# Revit family: 02-75-006 DN040-400
name_source: partatom
category: Pipe Accessories
units: mm (PartAtom-declared; Revit-internal decimal feet)

## family parameters
Always vertical = Yes
Cut with Voids When Loaded = No
Part Type = Valve - Breaks Into
Round Connector Dimension = Use Diameter
Shared = No
Work Plane-Based = No

## types (15) — shared parameters
1 = 1 mm  [stored 0.00328084 ft]
2 = 2 mm  [stored 0.00656168 ft]
5 = 5 mm  [stored 0.0164042 ft]
DN040_PN10/16 = 02-040-75-514649003
DN050_PN10/16 = 02-050-75-514649003
DN060/065_PN10/16 = 02-065-75-5L4649003
DN080_DIN1882 = 02-080-75-514649003
DN080_PN10/16 = 02-080-75-534649003
DN100_PN10/16 = 02-100-75-514649003
DN125_PN10/16 = 02-125-75-514649003
DN150_PN10/16 = 02-150-75-514649003
DN200_PN10 = 02-200-75-504649003
DN200_PN16 = 02-200-75-514649003
DN250_PN10 = 02-250-75-504649003
DN250_PN16 = 02-250-75-514649003
DN300_PN10 = 02-300-75-504647003
DN300_PN16 = 02-300-75-514647003
DN400_PN10 = 02-400-75-50464
DN400_PN16 = 02-400-75-51464
Description_ = AVK GATE VALVE, FLANGED, PN10/16
F = 14 mm  [stored 0.0459318 ft]
F1 = 15 mm  [stored 0.0492126 ft]
Search_table = 02-75-006 DN040-400
URL_product_pages = https://www.avkvalves.com
zero-valued in all types: Default Elevation

## per-type parameters (varying)
- DN040_PN10/16: Body_FL_L=60 mm; Body_FL_T=18 mm  [stored 0.0590551 ft]; Body_FL_W=45 mm; Body_H=95 mm; Body_L=45 mm; Body_R=14 mm  [stored 0.0459318 ft]; Body_T=5 mm  [stored 0.0164042 ft]; Body_W=30 mm  [stored 0.0984252 ft]; Bonnet_dim1=29 mm; Bonnet_dim2=17 mm  [stored 0.0557743 ft]; Bore=20 mm  [stored 0.0656168 ft]; DN=40 mm  [stored 0.131234 ft]; F0=14 mm  [stored 0.0459318 ft]; F11=16 mm  [stored 0.0524934 ft]; F2=42 mm; F22=30 mm  [stored 0.0984252 ft]; FL_R=25 mm  [stored 0.082021 ft]; FL_T=10 mm  [stored 0.0328084 ft]; H=226 mm; H1=164 mm; H3=301 mm; H3-H=75 mm; Increased_dim=60 mm; L=240 mm; L/2=120 mm; Logo height=81 mm; Nut=15 mm  [stored 0.0492126 ft]; Raised_Dia=58 mm; Raised_dis=3 mm  [stored 0.00984252 ft]; Reduced_dim1=33 mm  [stored 0.108268 ft]; Rib1=25 mm  [stored 0.082021 ft]; Rib2=40 mm  [stored 0.131234 ft]; Rib_H=25 mm  [stored 0.082021 ft]; Rib_L=52 mm; Rib_T=4 mm  [stored 0.0131234 ft]; Rib_W=35 mm  [stored 0.114829 ft]; Stand_Rib_W=38 mm  [stored 0.124672 ft]; Stem_R=23 mm; Stem_cap_H=53 mm; Stem_cap_dia=42 mm; disk_T=38 mm  [stored 0.124672 ft]
- DN060/065_PN10/16: Body_FL_L=86 mm; Body_FL_T=22 mm  [stored 0.0721785 ft]; Body_FL_W=48 mm; Body_H=102 mm; Body_L=74 mm; Body_R=18 mm  [stored 0.0590551 ft]; Body_T=6 mm  [stored 0.019685 ft]; Body_W=39 mm  [stored 0.127953 ft]; Bonnet_dim1=37 mm  [stored 0.121391 ft]; Bonnet_dim2=22 mm  [stored 0.0721785 ft]; Bore=33 mm  [stored 0.108268 ft]; DN=65 mm; F0=17 mm  [stored 0.0557743 ft]; F11=20 mm  [stored 0.0656168 ft]; F2=38 mm  [stored 0.124672 ft]; F22=34 mm  [stored 0.111549 ft]; FL_R=26 mm  [stored 0.0853018 ft]; FL_T=10 mm  [stored 0.0328084 ft]; H=301 mm; H1=205 mm; H3=394 mm; H3-H=93 mm; Increased_dim=74 mm; L=270 mm; L/2=135 mm; Logo height=86 mm; Nut=19 mm  [stored 0.062336 ft]; Raised_Dia=59 mm; Raised_dis=3 mm  [stored 0.00984252 ft]; Reduced_dim1=43 mm; Rib1=25 mm  [stored 0.082021 ft]; Rib2=51 mm; Rib_H=26 mm  [stored 0.0853018 ft]; Rib_L=85 mm; Rib_T=4 mm  [stored 0.0131234 ft]; Rib_W=45 mm; Stand_Rib_W=46 mm; Stem_R=31 mm  [stored 0.101706 ft]; Stem_cap_H=85 mm; Stem_cap_dia=56 mm; disk_T=49 mm
- DN080_DIN1882: Body_FL_L=86 mm; Body_FL_T=24 mm  [stored 0.0787402 ft]; Body_FL_W=48 mm; Body_H=108 mm; Body_L=72 mm; Body_R=16 mm  [stored 0.0524934 ft]; Body_T=7 mm  [stored 0.0229659 ft]; Body_W=35 mm  [stored 0.114829 ft]; Bonnet_dim1=33 mm  [stored 0.108268 ft]; Bonnet_dim2=20 mm  [stored 0.0656168 ft]; Bore=40 mm  [stored 0.131234 ft]; DN=80 mm; F0=17 mm  [stored 0.0557743 ft]; F11=20 mm  [stored 0.0656168 ft]; F2=38 mm  [stored 0.124672 ft]; F22=34 mm  [stored 0.111549 ft]; FL_R=26 mm  [stored 0.0853018 ft]; FL_T=10 mm  [stored 0.0328084 ft]; H=340 mm; H1=242 mm; H3=440 mm; H3-H=100 mm; Increased_dim=80 mm; L=280 mm; L/2=140 mm; Logo height=92 mm; Nut=17 mm  [stored 0.0557743 ft]; Raised_Dia=66 mm; Raised_dis=3 mm  [stored 0.00984252 ft]; Reduced_dim1=39 mm  [stored 0.127953 ft]; Rib1=25 mm  [stored 0.082021 ft]; Rib2=46 mm; Rib_H=28 mm  [stored 0.0918635 ft]; Rib_L=83 mm; Rib_T=4 mm  [stored 0.0131234 ft]; Rib_W=40 mm  [stored 0.131234 ft]; Stand_Rib_W=50 mm; Stem_R=31 mm  [stored 0.101706 ft]; Stem_cap_H=85 mm; Stem_cap_dia=56 mm; disk_T=44 mm
- DN080_PN10/16: Body_FL_L=86 mm; Body_FL_T=24 mm  [stored 0.0787402 ft]; Body_FL_W=48 mm; Body_H=108 mm; Body_L=72 mm; Body_R=16 mm  [stored 0.0524934 ft]; Body_T=7 mm  [stored 0.0229659 ft]; Body_W=35 mm  [stored 0.114829 ft]; Bonnet_dim1=33 mm  [stored 0.108268 ft]; Bonnet_dim2=20 mm  [stored 0.0656168 ft]; Bore=40 mm  [stored 0.131234 ft]; DN=80 mm; F0=17 mm  [stored 0.0557743 ft]; F11=20 mm  [stored 0.0656168 ft]; F2=38 mm  [stored 0.124672 ft]; F22=34 mm  [stored 0.111549 ft]; FL_R=26 mm  [stored 0.0853018 ft]; FL_T=10 mm  [stored 0.0328084 ft]; H=340 mm; H1=242 mm; H3=440 mm; H3-H=100 mm; Increased_dim=80 mm; L=280 mm; L/2=140 mm; Logo height=92 mm; Nut=17 mm  [stored 0.0557743 ft]; Raised_Dia=66 mm; Raised_dis=3 mm  [stored 0.00984252 ft]; Reduced_dim1=39 mm  [stored 0.127953 ft]; Rib1=25 mm  [stored 0.082021 ft]; Rib2=46 mm; Rib_H=28 mm  [stored 0.0918635 ft]; Rib_L=83 mm; Rib_T=4 mm  [stored 0.0131234 ft]; Rib_W=40 mm  [stored 0.131234 ft]; Stand_Rib_W=50 mm; Stem_R=31 mm  [stored 0.101706 ft]; Stem_cap_H=85 mm; Stem_cap_dia=56 mm; disk_T=44 mm
- DN100_PN10/16: Body_FL_L=96 mm; Body_FL_T=25 mm  [stored 0.082021 ft]; Body_FL_W=53 mm; Body_H=122 mm; Body_L=82 mm; Body_R=17 mm  [stored 0.0557743 ft]; Body_T=6 mm  [stored 0.019685 ft]; Body_W=38 mm  [stored 0.124672 ft]; Bonnet_dim1=36 mm; Bonnet_dim2=22 mm  [stored 0.0721785 ft]; Bore=50 mm; DN=100 mm; F0=19 mm  [stored 0.062336 ft]; F11=22 mm  [stored 0.0721785 ft]; F2=38 mm  [stored 0.124672 ft]; F22=34 mm  [stored 0.111549 ft]; FL_R=29 mm; FL_T=10 mm  [stored 0.0328084 ft]; H=355 mm; H1=257 mm; H3=465 mm; H3-H=110 mm; Increased_dim=88 mm; L=300 mm; L/2=150 mm; Logo height=104 mm; Nut=18 mm  [stored 0.0590551 ft]; Raised_Dia=78 mm; Raised_dis=3 mm  [stored 0.00984252 ft]; Reduced_dim1=42 mm; Rib1=25 mm  [stored 0.082021 ft]; Rib2=50 mm; Rib_H=32 mm  [stored 0.104987 ft]; Rib_L=94 mm; Rib_T=4 mm  [stored 0.0131234 ft]; Rib_W=44 mm; Stand_Rib_W=55 mm; Stem_R=31 mm  [stored 0.101706 ft]; Stem_cap_H=85 mm; Stem_cap_dia=56 mm; disk_T=48 mm
- DN125_PN10/16: Body_FL_L=110 mm; Body_FL_T=25 mm  [stored 0.082021 ft]; Body_FL_W=53 mm; Body_H=145 mm; Body_L=100 mm; Body_R=19 mm  [stored 0.062336 ft]; Body_T=6 mm  [stored 0.019685 ft]; Body_W=43 mm; Bonnet_dim1=41 mm; Bonnet_dim2=25 mm  [stored 0.082021 ft]; Bore=63 mm; DN=125 mm; F0=19 mm  [stored 0.062336 ft]; F11=22 mm  [stored 0.0721785 ft]; F2=38 mm  [stored 0.124672 ft]; F22=34 mm  [stored 0.111549 ft]; FL_R=29 mm; FL_T=15 mm  [stored 0.0492126 ft]; H=404 mm; H1=303 mm; H3=529 mm; H3-H=125 mm; Increased_dim=100 mm; L=325 mm; L/2=163 mm; Logo height=123 mm; Nut=21 mm  [stored 0.0688976 ft]; Raised_Dia=92 mm; Raised_dis=3 mm  [stored 0.00984252 ft]; Reduced_dim1=47 mm; Rib1=25 mm  [stored 0.082021 ft]; Rib2=57 mm; Rib_H=38 mm  [stored 0.124672 ft]; Rib_L=115 mm; Rib_T=5 mm  [stored 0.0164042 ft]; Rib_W=49 mm; Stand_Rib_W=63 mm; Stem_R=31 mm  [stored 0.101706 ft]; Stem_cap_H=85 mm; Stem_cap_dia=56 mm; disk_T=54 mm
- DN150_PN10/16: Body_FL_L=136 mm; Body_FL_T=25 mm  [stored 0.082021 ft]; Body_FL_W=75 mm; Body_H=172 mm; Body_L=122 mm; Body_R=22 mm  [stored 0.0721785 ft]; Body_T=6 mm  [stored 0.019685 ft]; Body_W=48 mm; Bonnet_dim1=46 mm; Bonnet_dim2=27 mm  [stored 0.0885827 ft]; Bore=75 mm; DN=150 mm; F0=19 mm  [stored 0.062336 ft]; F11=22 mm  [stored 0.0721785 ft]; F2=38 mm  [stored 0.124672 ft]; F22=34 mm  [stored 0.111549 ft]; FL_R=41 mm; FL_T=15 mm  [stored 0.0492126 ft]; H=458 mm; H1=354 mm; H3=600 mm; H3-H=142 mm; Increased_dim=114 mm; L=350 mm; L/2=175 mm; Logo height=146 mm; Nut=23 mm; Raised_Dia=106 mm; Raised_dis=3 mm  [stored 0.00984252 ft]; Reduced_dim1=53 mm; Rib1=25 mm  [stored 0.082021 ft]; Rib2=63 mm; Rib_H=45 mm; Rib_L=140 mm; Rib_T=5 mm  [stored 0.0164042 ft]; Rib_W=55 mm; Stand_Rib_W=71 mm; Stem_R=31 mm  [stored 0.101706 ft]; Stem_cap_H=85 mm; Stem_cap_dia=56 mm; disk_T=61 mm
- DN200_PN10: Body_FL_L=166 mm; Body_FL_T=30 mm  [stored 0.0984252 ft]; Body_FL_W=85 mm; Body_H=220 mm; Body_L=157 mm; Body_R=25 mm  [stored 0.082021 ft]; Body_T=7 mm  [stored 0.0229659 ft]; Body_W=55 mm; Bonnet_dim1=52 mm; Bonnet_dim2=31 mm  [stored 0.101706 ft]; Bore=100 mm; DN=200 mm; F0=24 mm  [stored 0.0787402 ft]; F11=28 mm  [stored 0.0918635 ft]; F2=38 mm  [stored 0.124672 ft]; F22=34 mm  [stored 0.111549 ft]; FL_R=47 mm; FL_T=20 mm  [stored 0.0656168 ft]; H=566 mm; H1=440 mm; H3=736 mm; H3-H=170 mm; Increased_dim=136 mm; L=400 mm; L/2=200 mm; Logo height=187 mm; Nut=27 mm  [stored 0.0885827 ft]; Raised_Dia=133 mm; Raised_dis=3 mm  [stored 0.00984252 ft]; Reduced_dim1=61 mm; Rib1=40 mm  [stored 0.131234 ft]; Rib2=73 mm; Rib_H=57 mm; Rib_L=181 mm; Rib_T=7 mm  [stored 0.0229659 ft]; Rib_W=63 mm; Stand_Rib_W=85 mm; Stem_R=39 mm  [stored 0.127953 ft]; Stem_cap_H=103 mm; Stem_cap_dia=70 mm; disk_T=70 mm
- DN200_PN16: Body_FL_L=166 mm; Body_FL_T=30 mm  [stored 0.0984252 ft]; Body_FL_W=85 mm; Body_H=220 mm; Body_L=157 mm; Body_R=25 mm  [stored 0.082021 ft]; Body_T=7 mm  [stored 0.0229659 ft]; Body_W=55 mm; Bonnet_dim1=52 mm; Bonnet_dim2=31 mm  [stored 0.101706 ft]; Bore=100 mm; DN=200 mm; F0=24 mm  [stored 0.0787402 ft]; F11=28 mm  [stored 0.0918635 ft]; F2=38 mm  [stored 0.124672 ft]; F22=34 mm  [stored 0.111549 ft]; FL_R=47 mm; FL_T=20 mm  [stored 0.0656168 ft]; H=566 mm; H1=440 mm; H3=736 mm; H3-H=170 mm; Increased_dim=136 mm; L=400 mm; L/2=200 mm; Logo height=187 mm; Nut=27 mm  [stored 0.0885827 ft]; Raised_Dia=133 mm; Raised_dis=3 mm  [stored 0.00984252 ft]; Reduced_dim1=61 mm; Rib1=40 mm  [stored 0.131234 ft]; Rib2=73 mm; Rib_H=57 mm; Rib_L=181 mm; Rib_T=7 mm  [stored 0.0229659 ft]; Rib_W=63 mm; Stand_Rib_W=85 mm; Stem_R=39 mm  [stored 0.127953 ft]; Stem_cap_H=103 mm; Stem_cap_dia=70 mm; disk_T=70 mm
- DN250_PN10: Body_FL_L=211 mm; Body_FL_T=30 mm  [stored 0.0984252 ft]; Body_FL_W=107 mm; Body_H=285 mm; Body_L=196 mm; Body_R=33 mm  [stored 0.108268 ft]; Body_T=9 mm  [stored 0.0295276 ft]; Body_W=73 mm; Bonnet_dim1=69 mm; Bonnet_dim2=41 mm; Bore=125 mm; DN=250 mm; F0=27 mm  [stored 0.0885827 ft]; F11=31 mm  [stored 0.101706 ft]; F2=38 mm  [stored 0.124672 ft]; F22=47 mm; FL_R=59 mm; FL_T=22 mm  [stored 0.0721785 ft]; H=688 mm; H1=556 mm; H3=888 mm; H3-H=200 mm; Increased_dim=160 mm; L=450 mm; L/2=225 mm; Logo height=242 mm; Nut=35 mm  [stored 0.114829 ft]; Raised_Dia=160 mm; Raised_dis=2 mm  [stored 0.00656168 ft]; Reduced_dim1=80 mm; Rib1=40 mm  [stored 0.131234 ft]; Rib2=96 mm; Rib_H=74 mm; Rib_L=225 mm; Rib_T=8 mm  [stored 0.0262467 ft]; Rib_W=83 mm; Stand_Rib_W=100 mm; Stem_R=39 mm  [stored 0.127953 ft]; Stem_cap_H=103 mm; Stem_cap_dia=70 mm; disk_T=92 mm
- DN250_PN16: Body_FL_L=211 mm; Body_FL_T=30 mm  [stored 0.0984252 ft]; Body_FL_W=107 mm; Body_H=285 mm; Body_L=196 mm; Body_R=33 mm  [stored 0.108268 ft]; Body_T=9 mm  [stored 0.0295276 ft]; Body_W=73 mm; Bonnet_dim1=69 mm; Bonnet_dim2=41 mm; Bore=125 mm; DN=250 mm; F0=27 mm  [stored 0.0885827 ft]; F11=31 mm  [stored 0.101706 ft]; F2=38 mm  [stored 0.124672 ft]; F22=47 mm; FL_R=59 mm; FL_T=22 mm  [stored 0.0721785 ft]; H=688 mm; H1=556 mm; H3=888 mm; H3-H=200 mm; Increased_dim=160 mm; L=450 mm; L/2=225 mm; Logo height=242 mm; Nut=35 mm  [stored 0.114829 ft]; Raised_Dia=160 mm; Raised_dis=2 mm  [stored 0.00656168 ft]; Reduced_dim1=80 mm; Rib1=40 mm  [stored 0.131234 ft]; Rib2=96 mm; Rib_H=74 mm; Rib_L=225 mm; Rib_T=8 mm  [stored 0.0262467 ft]; Rib_W=83 mm; Stand_Rib_W=100 mm; Stem_R=39 mm  [stored 0.127953 ft]; Stem_cap_H=103 mm; Stem_cap_dia=70 mm; disk_T=92 mm
- DN300_PN10: Body_FL_L=228 mm; Body_FL_T=45 mm; Body_FL_W=116 mm; Body_H=370 mm; Body_L=205 mm; Body_R=38 mm  [stored 0.124672 ft]; Body_T=9 mm  [stored 0.0295276 ft]; Body_W=85 mm; Bonnet_dim1=81 mm; Bonnet_dim2=48 mm; Bore=150 mm; DN=300 mm; F0=27 mm  [stored 0.0885827 ft]; F11=31 mm  [stored 0.101706 ft]; F2=38 mm  [stored 0.124672 ft]; F22=47 mm; FL_R=64 mm; FL_T=25 mm  [stored 0.082021 ft]; H=772 mm; H1=636 mm; H3=999 mm; H3-H=227 mm; Increased_dim=182 mm; L=500 mm; L/2=250 mm; Logo height=315 mm; Nut=41 mm; Raised_Dia=185 mm; Raised_dis=2 mm  [stored 0.00656168 ft]; Reduced_dim1=94 mm; Rib1=98 mm; Rib2=228 mm; Rib_H=96 mm; Rib_L=236 mm; Rib_T=9 mm  [stored 0.0295276 ft]; Rib_W=98 mm; Stand_Rib_W=114 mm; Stem_R=39 mm  [stored 0.127953 ft]; Stem_cap_H=103 mm; Stem_cap_dia=70 mm; disk_T=108 mm
- DN300_PN16: Body_FL_L=228 mm; Body_FL_T=45 mm; Body_FL_W=116 mm; Body_H=370 mm; Body_L=205 mm; Body_R=38 mm  [stored 0.124672 ft]; Body_T=9 mm  [stored 0.0295276 ft]; Body_W=85 mm; Bonnet_dim1=81 mm; Bonnet_dim2=48 mm; Bore=150 mm; DN=300 mm; F0=27 mm  [stored 0.0885827 ft]; F11=31 mm  [stored 0.101706 ft]; F2=38 mm  [stored 0.124672 ft]; F22=47 mm; FL_R=64 mm; FL_T=25 mm  [stored 0.082021 ft]; H=772 mm; H1=636 mm; H3=999 mm; H3-H=227 mm; Increased_dim=182 mm; L=500 mm; L/2=250 mm; Logo height=315 mm; Nut=41 mm; Raised_Dia=185 mm; Raised_dis=2 mm  [stored 0.00656168 ft]; Reduced_dim1=94 mm; Rib1=98 mm; Rib2=228 mm; Rib_H=96 mm; Rib_L=236 mm; Rib_T=9 mm  [stored 0.0295276 ft]; Rib_W=98 mm; Stand_Rib_W=114 mm; Stem_R=39 mm  [stored 0.127953 ft]; Stem_cap_H=103 mm; Stem_cap_dia=70 mm; disk_T=108 mm
- DN400_PN10: Body_FL_L=290 mm; Body_FL_T=60 mm; Body_FL_W=125 mm; Body_H=512 mm; Body_L=238 mm; Body_R=39 mm  [stored 0.127953 ft]; Body_T=13 mm; Body_W=86 mm; Bonnet_dim1=82 mm; Bonnet_dim2=49 mm; Bore=200 mm; DN=400 mm; F0=32 mm  [stored 0.104987 ft]; F11=37 mm  [stored 0.121391 ft]; F2=38 mm  [stored 0.124672 ft]; F22=55 mm; FL_R=69 mm; FL_T=25 mm  [stored 0.082021 ft]; H=1017 mm; H1=857 mm; H3=1307 mm; H3-H=290 mm; Increased_dim=232 mm; L=600 mm; L/2=300 mm; Logo height=435 mm; Nut=42 mm; Raised_Dia=240 mm; Raised_dis=4 mm  [stored 0.0131234 ft]; Reduced_dim1=95 mm; Rib1=99 mm; Rib2=274 mm; Rib_H=133 mm; Rib_L=274 mm; Rib_T=9 mm  [stored 0.0295276 ft]; Rib_W=99 mm; Stand_Rib_W=145 mm; Stem_R=41 mm; Stem_cap_H=115 mm; Stem_cap_dia=75 mm; disk_T=109 mm
- DN400_PN16: Body_FL_L=290 mm; Body_FL_T=60 mm; Body_FL_W=125 mm; Body_H=512 mm; Body_L=238 mm; Body_R=39 mm  [stored 0.127953 ft]; Body_T=13 mm; Body_W=86 mm; Bonnet_dim1=82 mm; Bonnet_dim2=49 mm; Bore=200 mm; DN=400 mm; F0=32 mm  [stored 0.104987 ft]; F11=37 mm  [stored 0.121391 ft]; F2=38 mm  [stored 0.124672 ft]; F22=55 mm; FL_R=69 mm; FL_T=28 mm  [stored 0.0918635 ft]; H=1017 mm; H1=857 mm; H3=1307 mm; H3-H=290 mm; Increased_dim=232 mm; L=600 mm; L/2=300 mm; Logo height=435 mm; Nut=42 mm; Raised_Dia=240 mm; Raised_dis=4 mm  [stored 0.0131234 ft]; Reduced_dim1=95 mm; Rib1=99 mm; Rib2=274 mm; Rib_H=133 mm; Rib_L=274 mm; Rib_T=10 mm  [stored 0.0328084 ft]; Rib_W=99 mm; Stand_Rib_W=145 mm; Stem_R=41 mm; Stem_cap_H=115 mm; Stem_cap_dia=75 mm; disk_T=109 mm

note: [stored X ft] marks values corroborated as IEEE doubles in the binary element streams (Revit-internal decimal feet)

## geometry (parser evidence)
native form markers: Sweep x2
no freeform markers — native parametric forms only
